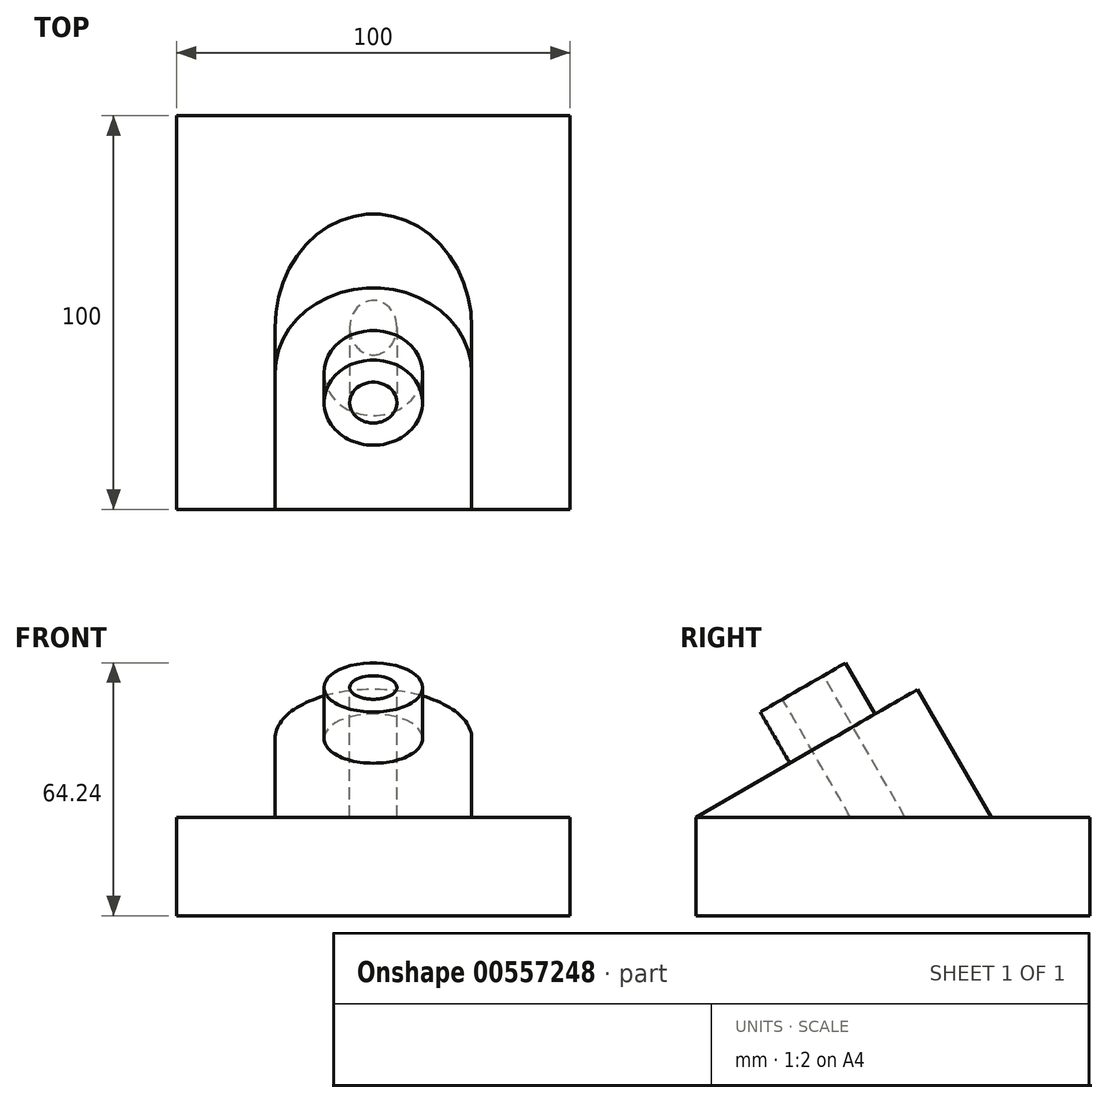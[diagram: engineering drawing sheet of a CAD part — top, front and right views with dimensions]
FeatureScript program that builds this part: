
annotation { "Feature Type Name" : "Feature", "Feature Type Description" : "" }
export const myFeature = defineFeature(function(context is Context, id is Id, definition is map)
    precondition{}
    {
        {
            var Q0;
            Q0=qCreatedBy(makeId("Top.planeOp"),FACE);
            var sketch = newSketch(context, id + "F0", { "sketchPlane" : qUnion([Q0])});
            skLineSegment(sketch, "E0.bottom", {"start": v(50, 50) * mm, "end": v(-50, 50) * mm});
            skLineSegment(sketch, "E0.top", {"start": v(50, -50) * mm, "end": v(-50, -50) * mm});
            skLineSegment(sketch, "E0.left", {"start": v(50, 50) * mm, "end": v(50, -50) * mm});
            skLineSegment(sketch, "E0.right", {"start": v(-50, 50) * mm, "end": v(-50, -50) * mm});
            skPoint(sketch, "E0.middle", {"position": v(0, 0) * mm});
            skSolve(sketch);
        }
        {
            var Q0;
            Q0=makeQuery(id+"F0.imprint","IMPRINT",FACE,{"disambiguationData":[TD([[makeQuery(id+"F0.imprint","IMPRINT",EDGE,{"derivedFrom":sQuery(id+"F0.wireOp",EDGE,"E0.bottom")}),1.0]])]});
            extrude(context, id + "F1", {"entities" : qUnion([Q0]), "depth" : 25 * mm, "offsetDistance" : 25 * mm});
        }
        {
            var Q0;
            Q0=qCreatedBy(makeId("Right.planeOp"),FACE);
            var sketch = newSketch(context, id + "F2", { "sketchPlane" : qUnion([Q0])});
            skLineSegment(sketch, "E1", {"start": v(-50, 25) * mm, "end": v(-11.36, 47.3) * mm});
            skSolve(sketch);
        }
        {
            var Q0;
            Q0=sQuery(id+"F2.wireOp",VERTEX,"E1.end");
            var Q1;
            Q1=makeQuery(id+"F1.opExtrude","CAP_VERTEX",VERTEX,{"disambiguationData":[OSD([sQuery(id+"F0.wireOp",EDGE,"E0.top"),sQuery(id+"F0.wireOp",EDGE,"E0.left")])],"isStart":false});
            var Q2;
            Q2=makeQuery(id+"F1.opExtrude","CAP_VERTEX",VERTEX,{"disambiguationData":[OSD([sQuery(id+"F0.wireOp",EDGE,"E0.top"),sQuery(id+"F0.wireOp",EDGE,"E0.right")])],"isStart":false});
            cPlane(context, id + "F3", {"entities" : qUnion([Q0, Q1, Q2]), "cplaneType" : CPlaneType.THREE_POINT, "offset" : 25 * mm, "width" : 150 * mm, "height" : 150 * mm});
        }
        {
            var Q0;
            Q0=qCreatedBy(id+"F3.planeOp",FACE);
            var sketch = newSketch(context, id + "F4", { "sketchPlane" : qUnion([Q0])});
            skLineSegment(sketch, "E2.bottom", {"start": v(-25, -30.8) * mm, "end": v(25, -30.8) * mm});
            skLineSegment(sketch, "E2.left", {"start": v(-25, -30.8) * mm, "end": v(-25, 9.2) * mm});
            skLineSegment(sketch, "E2.right", {"start": v(25, -30.8) * mm, "end": v(25, 9.2) * mm});
            skArc(sketch, "E3", {"start": v(-25, 9.2) * mm, "mid": v(0, 34.2) * mm, "end": v(25, 9.2) * mm});
            skSolve(sketch);
        }
        {
            var Q0;
            Q0 = qSketchRegion(id + "F4", true);
            var Q1;
            Q1=makeQuery(id+"F1.opExtrude","CAP_FACE",FACE,{"disambiguationData":[OSD([sQuery(id+"F0.wireOp",EDGE,"E0.bottom"),sQuery(id+"F0.wireOp",EDGE,"E0.top"),sQuery(id+"F0.wireOp",EDGE,"E0.left"),sQuery(id+"F0.wireOp",EDGE,"E0.right")])],"isStart":false});
            extrude(context, id + "F5", {"entities" : qUnion([Q0]), "operationType" : NewBodyOperationType.ADD, "endBound" : BoundingType.UP_TO_SURFACE, "oppositeDirection" : true, "depth" : 25 * mm, "endBoundEntityFace" : qUnion([Q1]), "offsetDistance" : 25 * mm});
        }
        {
            var Q0;
            Q0=makeQuery(id+"F5.opExtrude","CAP_FACE",FACE,{"disambiguationData":[OSD([sQuery(id+"F4.wireOp",EDGE,"E2.bottom"),sQuery(id+"F4.wireOp",EDGE,"E2.left"),sQuery(id+"F4.wireOp",EDGE,"E2.right"),sQuery(id+"F4.wireOp",EDGE,"E3")])],"isStart":true});
            var sketch = newSketch(context, id + "F6", { "sketchPlane" : qUnion([Q0])});
            skCircle(sketch, "E4", {"center": v(0, 9.2) * mm, "radius": 12.5 * mm});
            skSolve(sketch);
        }
        {
            var Q0;
            Q0=makeQuery(id+"F6.imprint","IMPRINT",FACE,{"disambiguationData":[TD([[makeQuery(id+"F6.imprint","IMPRINT",EDGE,{"derivedFrom":sQuery(id+"F6.wireOp",EDGE,"E4")}),1.0]])]});
            extrude(context, id + "F7", {"entities" : qUnion([Q0]), "operationType" : NewBodyOperationType.ADD, "depth" : 15 * mm, "offsetDistance" : 25 * mm});
        }
        {
            var Q0;
            Q0=makeQuery(id+"F7.opExtrude","CAP_FACE",FACE,{"disambiguationData":[OSD([sQuery(id+"F6.wireOp",EDGE,"E4")])],"isStart":false});
            var sketch = newSketch(context, id + "F8", { "sketchPlane" : qUnion([Q0])});
            skCircle(sketch, "E5", {"center": v(0, 9.2) * mm, "radius": 6 * mm});
            skSolve(sketch);
        }
        {
            var Q0;
            Q0=makeQuery(id+"F8.imprint","IMPRINT",FACE,{"disambiguationData":[TD([[makeQuery(id+"F8.imprint","IMPRINT",EDGE,{"derivedFrom":sQuery(id+"F8.wireOp",EDGE,"E5")}),1.0]])]});
            var Q1;
            Q1=makeQuery(id+"F1.opExtrude","CAP_FACE",FACE,{"disambiguationData":[OSD([sQuery(id+"F0.wireOp",EDGE,"E0.bottom"),sQuery(id+"F0.wireOp",EDGE,"E0.top"),sQuery(id+"F0.wireOp",EDGE,"E0.left"),sQuery(id+"F0.wireOp",EDGE,"E0.right")])],"isStart":false});
            extrude(context, id + "F9", {"entities" : qUnion([Q0]), "operationType" : NewBodyOperationType.REMOVE, "endBound" : BoundingType.UP_TO_SURFACE, "oppositeDirection" : true, "depth" : 25 * mm, "endBoundEntityFace" : qUnion([Q1]), "offsetDistance" : 25 * mm});
        }
    });
